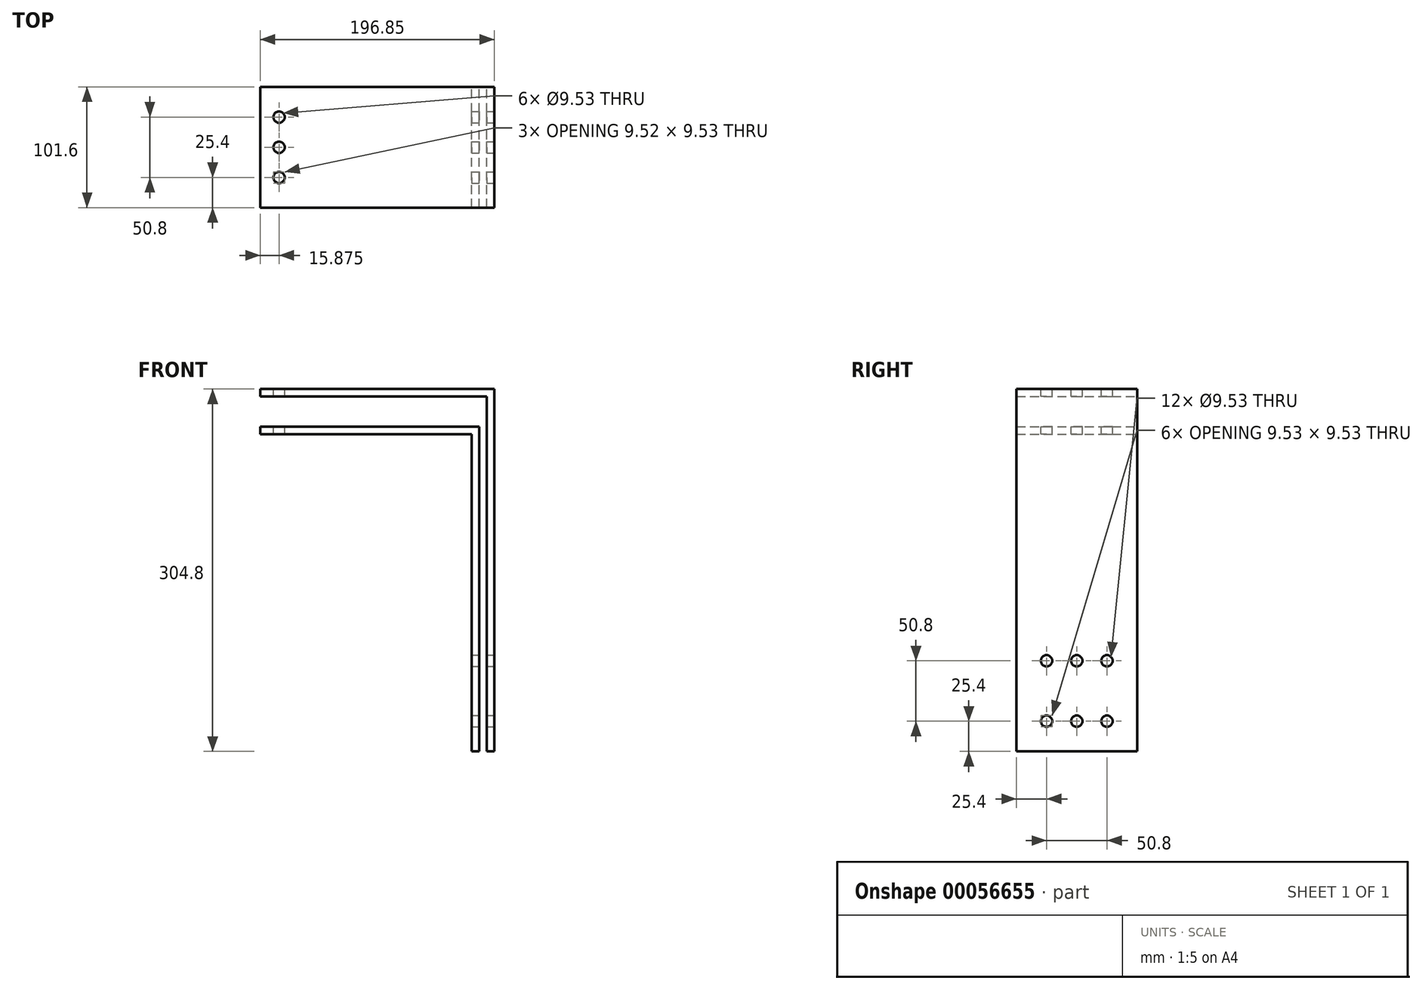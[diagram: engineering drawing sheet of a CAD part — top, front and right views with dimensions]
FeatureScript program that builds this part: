
annotation { "Feature Type Name" : "Feature", "Feature Type Description" : "" }
export const myFeature = defineFeature(function(context is Context, id is Id, definition is map)
    precondition{}
    {
        {
            var Q0;
            Q0=qCreatedBy(makeId("Front.planeOp"),FACE);
            var sketch = newSketch(context, id + "F0", { "sketchPlane" : qUnion([Q0])});
            skLineSegment(sketch, "E0", {"start": v(0, -31.75) * mm, "end": v(184.15, -31.75) * mm});
            skLineSegment(sketch, "E1", {"start": v(184.15, -31.75) * mm, "end": v(184.15, -304.8) * mm});
            skLineSegment(sketch, "E2", {"start": v(177.8, -38.1) * mm, "end": v(0, -38.1) * mm});
            skLineSegment(sketch, "E3", {"start": v(190.5, -6.35) * mm, "end": v(0, -6.35) * mm});
            skLineSegment(sketch, "E4", {"start": v(0, -6.35) * mm, "end": v(0, 0) * mm});
            skLineSegment(sketch, "E5", {"start": v(0, 0) * mm, "end": v(196.85, 0) * mm});
            skLineSegment(sketch, "E6", {"start": v(196.85, 0) * mm, "end": v(196.85, -304.8) * mm});
            skLineSegment(sketch, "E7", {"start": v(177.8, -304.8) * mm, "end": v(184.15, -304.8) * mm});
            skLineSegment(sketch, "E8.trimOffspring", {"start": v(177.8, -304.8) * mm, "end": v(177.8, -38.1) * mm});
            skLineSegment(sketch, "E9.trimOffspring", {"start": v(190.5, -304.8) * mm, "end": v(190.5, -6.35) * mm});
            skLineSegment(sketch, "E10.trimOffspring", {"start": v(190.5, -304.8) * mm, "end": v(196.85, -304.8) * mm});
            skLineSegment(sketch, "E11", {"start": v(0, -31.75) * mm, "end": v(0, -38.1) * mm});
            skSolve(sketch);
        }
        {
            var Q0;
            Q0=qSketchRegion(id+"F0",true);
            extrude(context, id + "F1", {"entities" : qUnion([Q0]), "endBound" : BoundingType.SYMMETRIC, "depth" : 101.6 * mm});
        }
        {
            var Q0;
            Q0=makeQuery(id+"F1.opExtrude","SWEPT_FACE",FACE,{"disambiguationData":[OSD([sQuery(id+"F0.wireOp",EDGE,"E6")])]});
            var sketch = newSketch(context, id + "F2", { "sketchPlane" : qUnion([Q0])});
            skCircle(sketch, "E12", {"center": v(-25.4, -279.4) * mm, "radius": 4.76 * mm});
            skCircle(sketch, "E13.0.1.0", {"center": v(-25.4, -228.6) * mm, "radius": 4.76 * mm});
            skCircle(sketch, "E13.1.0.0", {"center": v(0, -279.4) * mm, "radius": 4.76 * mm});
            skCircle(sketch, "E13.1.1.0", {"center": v(0, -228.6) * mm, "radius": 4.76 * mm});
            skCircle(sketch, "E13.2.0.0", {"center": v(25.4, -279.4) * mm, "radius": 4.76 * mm});
            skCircle(sketch, "E13.2.1.0", {"center": v(25.4, -228.6) * mm, "radius": 4.76 * mm});
            skLineSegment(sketch, "E13.direction1", {"start": v(-25.4, -279.4) * mm, "end": v(0, -279.4) * mm, "construction": true});
            skLineSegment(sketch, "E13.direction2", {"start": v(-25.4, -279.4) * mm, "end": v(-25.4, -228.6) * mm, "construction": true});
            skSolve(sketch);
        }
        {
            var Q0;
            Q0=qSketchRegion(id+"F2",true);
            extrude(context, id + "F3", {"entities" : qUnion([Q0]), "operationType" : NewBodyOperationType.REMOVE, "endBound" : BoundingType.THROUGH_ALL, "oppositeDirection" : true, "depth" : 25.4 * mm});
        }
        {
            var Q0;
            Q0=makeQuery(id+"F1.opExtrude","SWEPT_FACE",FACE,{"disambiguationData":[OSD([sQuery(id+"F0.wireOp",EDGE,"E5")])]});
            var sketch = newSketch(context, id + "F4", { "sketchPlane" : qUnion([Q0])});
            skCircle(sketch, "E14", {"center": v(15.88, -25.4) * mm, "radius": 4.76 * mm});
            skCircle(sketch, "E15.0.1.0", {"center": v(15.88, 0) * mm, "radius": 4.76 * mm});
            skCircle(sketch, "E15.0.2.0", {"center": v(15.88, 25.4) * mm, "radius": 4.76 * mm});
            skLineSegment(sketch, "E15.direction1", {"start": v(-97.7, -25.4) * mm, "end": v(15.88, -25.4) * mm, "construction": true});
            skLineSegment(sketch, "E15.direction2", {"start": v(15.88, -25.4) * mm, "end": v(15.88, 0) * mm, "construction": true});
            skSolve(sketch);
        }
        {
            var Q0;
            Q0=qSketchRegion(id+"F4",true);
            extrude(context, id + "F5", {"entities" : qUnion([Q0]), "operationType" : NewBodyOperationType.REMOVE, "endBound" : BoundingType.THROUGH_ALL, "oppositeDirection" : true, "depth" : 25.4 * mm});
        }
    });
